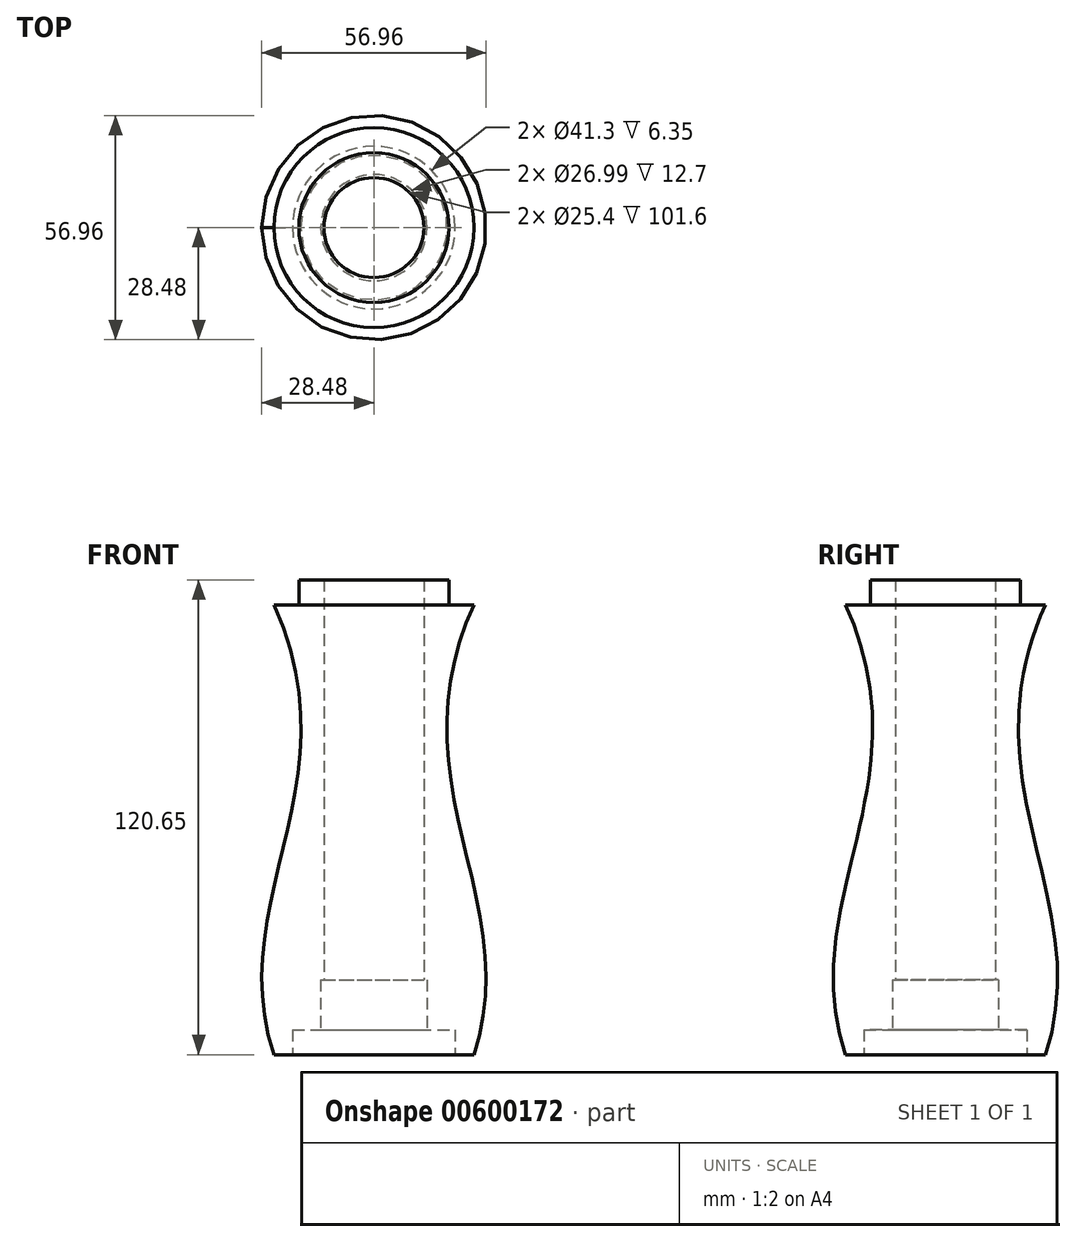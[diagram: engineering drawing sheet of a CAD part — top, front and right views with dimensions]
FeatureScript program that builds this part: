
annotation { "Feature Type Name" : "Feature", "Feature Type Description" : "" }
export const myFeature = defineFeature(function(context is Context, id is Id, definition is map)
    precondition{}
    {
        {
            var Q0;
            Q0=qCreatedBy(makeId("Front.planeOp"),FACE);
            var sketch = newSketch(context, id + "F0", { "sketchPlane" : qUnion([Q0])});
            skLineSegment(sketch, "E0.0", {"start": v(-12.7, 19.05) * mm, "end": v(-12.7, 114.3) * mm});
            skFitSpline(sketch, "E1", {"points": [v(-25.4, 114.3) * mm, v(-25.41, 0) * mm], "startDerivative": vector(62.05, -136.64) * mm, "endDerivative": vector(38.94, -118.3) * mm});
            skLineSegment(sketch, "E2", {"start": v(-25.41, 0) * mm, "end": v(-20.65, 0) * mm});
            skLineSegment(sketch, "E3", {"start": v(-25.4, 114.3) * mm, "end": v(-19.05, 114.3) * mm});
            skLineSegment(sketch, "E4.0", {"start": v(-19.05, 114.3) * mm, "end": v(-19.05, 120.65) * mm});
            skLineSegment(sketch, "E5.0", {"start": v(-19.05, 120.65) * mm, "end": v(-12.7, 120.65) * mm});
            skLineSegment(sketch, "E6", {"start": v(-12.7, 114.3) * mm, "end": v(-12.7, 120.65) * mm});
            skLineSegment(sketch, "E7.0", {"start": v(-20.65, 0) * mm, "end": v(-20.65, 6.35) * mm});
            skLineSegment(sketch, "E8.0", {"start": v(-20.65, 6.35) * mm, "end": v(-13.5, 6.35) * mm});
            skLineSegment(sketch, "E9.0", {"start": v(-13.5, 19.05) * mm, "end": v(-12.7, 19.05) * mm});
            skLineSegment(sketch, "E10.0", {"start": v(-13.5, 6.35) * mm, "end": v(-13.5, 19.05) * mm});
            skLineSegment(sketch, "E11", {"start": v(0, 0) * mm, "end": v(0, 104.62) * mm});
            skLineSegment(sketch, "E12", {"start": v(-20.65, 0) * mm, "end": v(0, 0) * mm, "construction": true});
            skSolve(sketch);
        }
        {
            var Q0;
            Q0=makeQuery(id+"F0.imprint","IMPRINT",FACE,{"disambiguationData":[TD([[makeQuery(id+"F0.imprint","IMPRINT",EDGE,{"derivedFrom":sQuery(id+"F0.wireOp",EDGE,"E0.0")}),1.0]])]});
            var Q1;
            Q1=sQuery(id+"F0.wireOp",EDGE,"E11");
            revolve(context, id + "F1", {"entities" : qUnion([Q0]), "axis" : qUnion([Q1]), "revolveType" : RevolveType.FULL});
        }
    });
